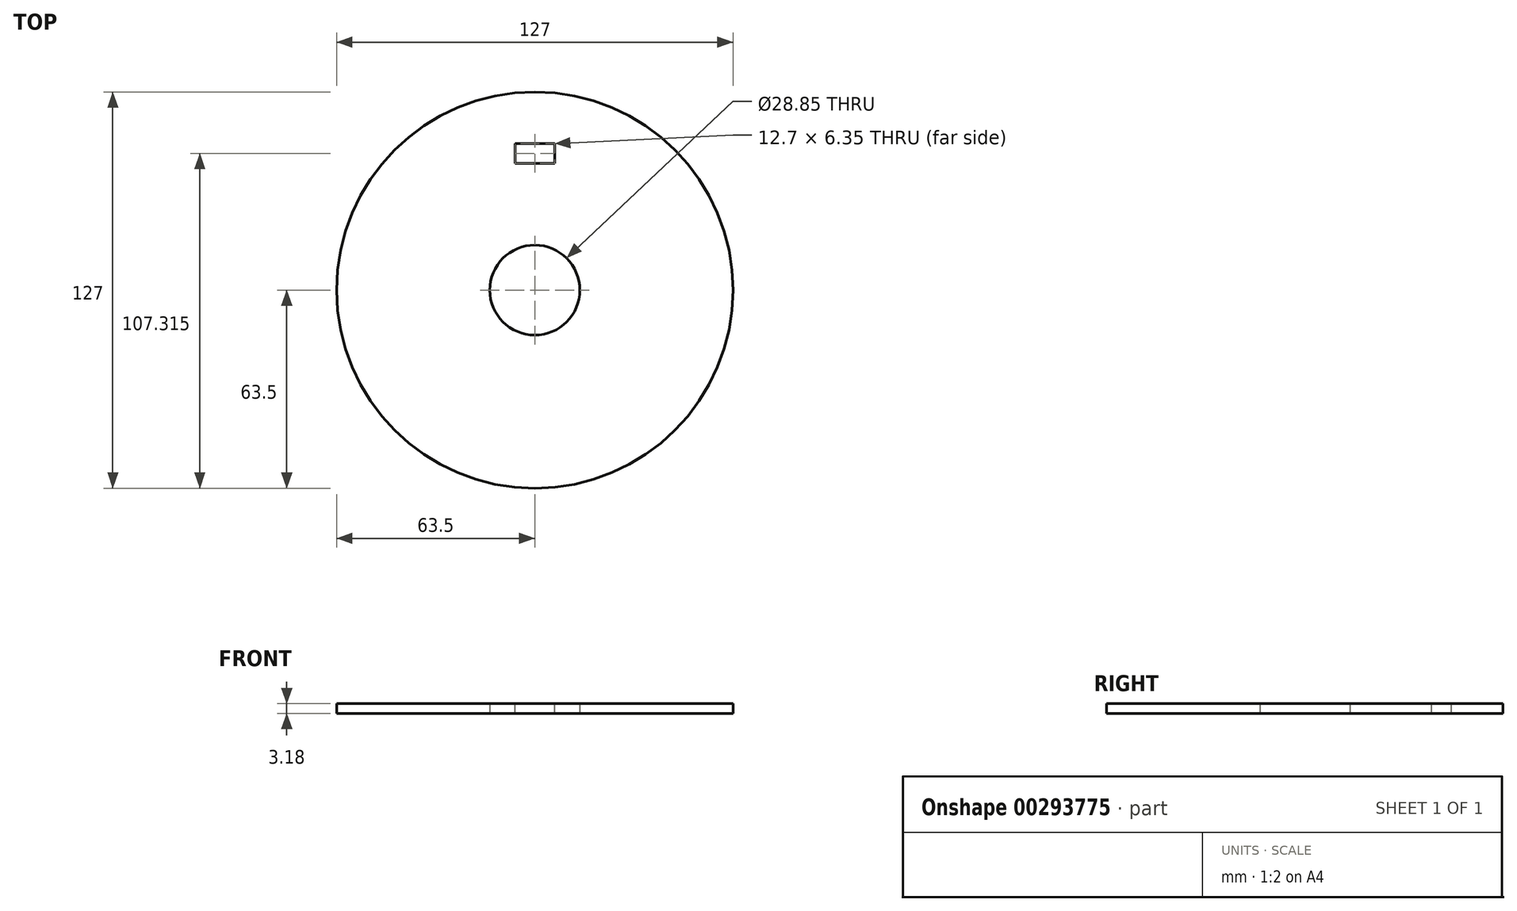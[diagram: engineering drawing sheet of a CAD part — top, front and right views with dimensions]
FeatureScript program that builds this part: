
annotation { "Feature Type Name" : "Feature", "Feature Type Description" : "" }
export const myFeature = defineFeature(function(context is Context, id is Id, definition is map)
    precondition{}
    {
        {
            var Q0;
            Q0=qCreatedBy(makeId("Top.planeOp"),FACE);
            var sketch = newSketch(context, id + "F0", { "sketchPlane" : qUnion([Q0])});
            skCircle(sketch, "E0", {"center": v(0, 0) * mm, "radius": 63.5 * mm});
            skCircle(sketch, "E1", {"center": v(0, 0) * mm, "radius": 14.43 * mm});
            skSolve(sketch);
        }
        {
            var Q0;
            Q0=makeQuery(id+"F0.imprint","IMPRINT",FACE,{"disambiguationData":[TD([[makeQuery(id+"F0.imprint","IMPRINT",EDGE,{"derivedFrom":sQuery(id+"F0.wireOp",EDGE,"E0")}),1.0]])]});
            extrude(context, id + "F1", {"entities" : qUnion([Q0]), "depth" : 3.17 * mm});
        }
        {
            var Q0;
            Q0=makeQuery(id+"F1.opExtrude","CAP_FACE",FACE,{"disambiguationData":[OSD([sQuery(id+"F0.wireOp",EDGE,"E0"),sQuery(id+"F0.wireOp",EDGE,"E1")])],"isStart":false});
            var sketch = newSketch(context, id + "F2", { "sketchPlane" : qUnion([Q0])});
            skLineSegment(sketch, "E2.bottom", {"start": v(6.35, 47) * mm, "end": v(-6.35, 47) * mm});
            skLineSegment(sketch, "E2.top", {"start": v(6.35, 40.64) * mm, "end": v(-6.35, 40.64) * mm});
            skLineSegment(sketch, "E2.left", {"start": v(6.35, 47) * mm, "end": v(6.35, 40.64) * mm});
            skLineSegment(sketch, "E2.right", {"start": v(-6.35, 47) * mm, "end": v(-6.35, 40.64) * mm});
            skPoint(sketch, "E2.middle", {"position": v(0, 43.82) * mm});
            skSolve(sketch);
        }
        {
            var Q0;
            Q0 = qSketchRegion(id + "F2", true);
            extrude(context, id + "F3", {"entities" : qUnion([Q0]), "operationType" : NewBodyOperationType.REMOVE, "endBound" : BoundingType.THROUGH_ALL, "oppositeDirection" : true, "depth" : 25.4 * mm});
        }
        {
            var Q0;
            Q0=qCreatedBy(makeId("Top.planeOp"),FACE);
            var sketch = newSketch(context, id + "F4", { "sketchPlane" : qUnion([Q0])});
            skCircle(sketch, "E3", {"center": v(0, 23.81) * mm, "radius": 2.49 * mm});
            skSolve(sketch);
        }
        {
            var Q0;
            Q0 = qSketchRegion(id + "F4", true);
            extrude(context, id + "F5", {"entities" : qUnion([Q0]), "operationType" : NewBodyOperationType.REMOVE, "endBound" : BoundingType.THROUGH_ALL, "oppositeDirection" : true, "depth" : 25.4 * mm});
        }
    });
